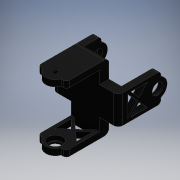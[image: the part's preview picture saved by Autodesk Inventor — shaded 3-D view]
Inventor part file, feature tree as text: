
AUTODESK INVENTOR PART (.ipt)
format: ipt  version: 2016 (Build 200138000, 138)  size: 391,680 bytes
history: native  units: mm
features: extrude x14, sketch x14, fillet x2, other x1
ambient origin geometry x8: Origin, YZ Plane, XZ Plane, XY Plane, X Axis, Y Axis, Z Axis, Center Point
bodies: Body1 (feature_tree)
feature tree (31):
  other  "ソリッド1"
  extrude  "押し出し1"  Depth=18.0mm
  extrude  "押し出し2"  Depth=41.8mm
  extrude  "押し出し3"  Depth=41.8mm
  extrude  "押し出し4"  Depth=18.0mm
  extrude  "押し出し5"  Depth=6.0mm TaperAngle=0.0deg
  extrude  "押し出し6"  Depth=4.0mm
  extrude  "押し出し7"  Depth=4.0mm
  extrude  "押し出し8"  Depth=25.0mm TaperAngle=0.0deg
  extrude  "押し出し9"  Depth=4.0mm
  extrude  "押し出し10"  Depth=4.0mm
  extrude  "押し出し11"  Depth=25.0mm TaperAngle=0.0deg
  extrude  "押し出し12"  Depth=25.0mm
  extrude  "押し出し13"  Depth=12.0mm
  extrude  "押し出し14"  Depth=2.0mm
  fillet  "フィレット1"  Radius=2.0mm
  fillet  "フィレット2"  Radius=6.0mm
  sketch  "スケッチ1"
  sketch  "スケッチ2"
  sketch  "スケッチ3"
  sketch  "スケッチ4"
  sketch  "スケッチ5"
  sketch  "スケッチ6"
  sketch  "スケッチ7"
  sketch  "スケッチ8"
  sketch  "スケッチ9"
  sketch  "スケッチ10"
  sketch  "スケッチ11"
  sketch  "スケッチ12"
  sketch  "スケッチ13"
  sketch  "スケッチ14"
